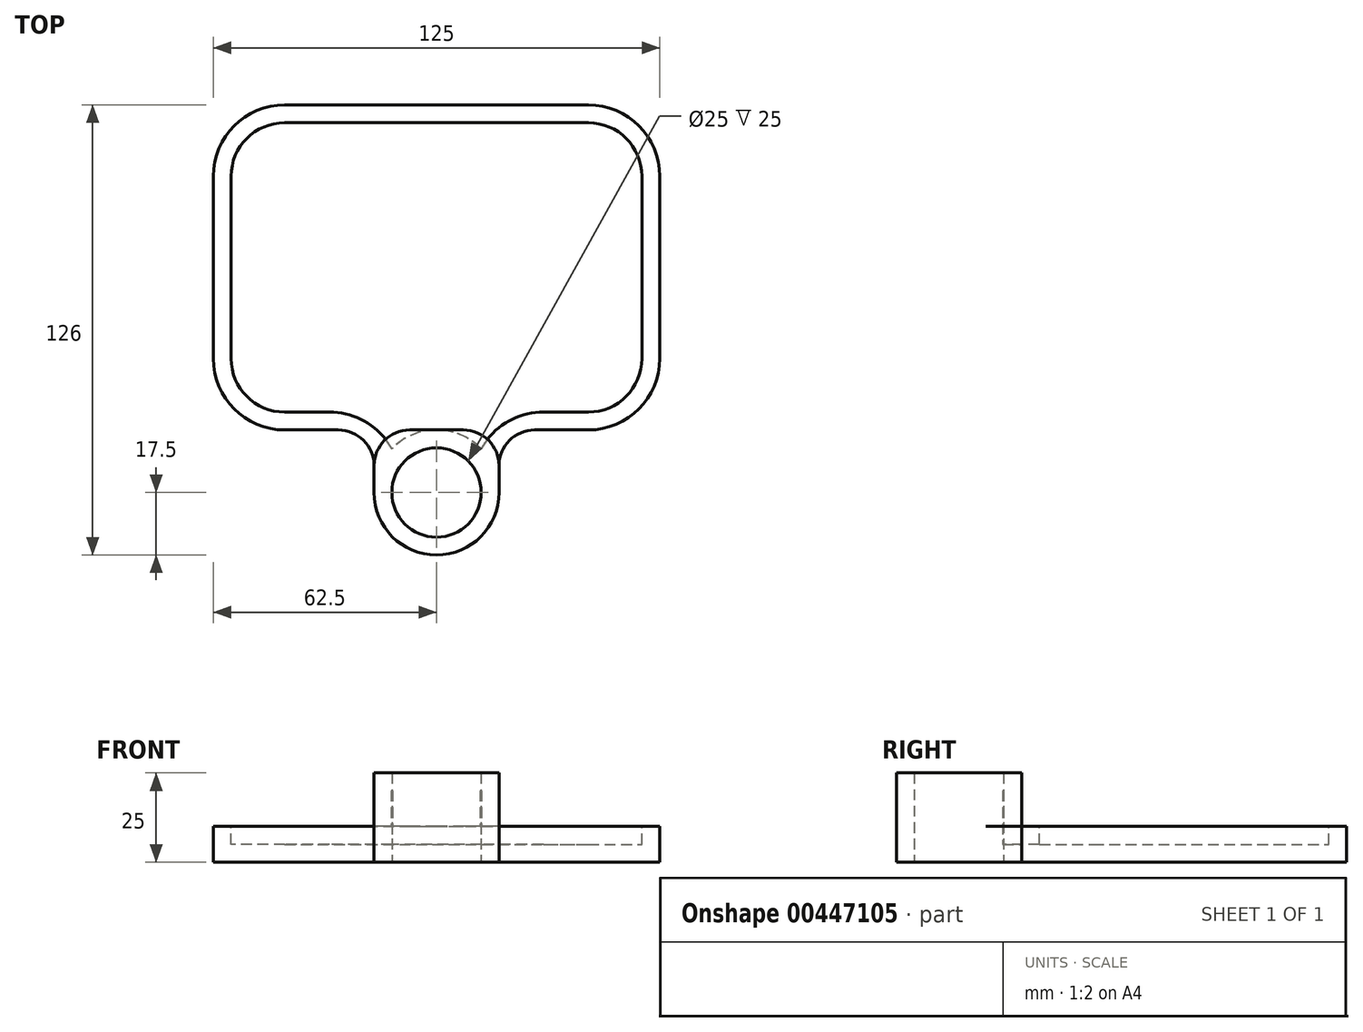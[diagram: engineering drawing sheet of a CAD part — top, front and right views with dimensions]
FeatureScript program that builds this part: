
annotation { "Feature Type Name" : "Feature", "Feature Type Description" : "" }
export const myFeature = defineFeature(function(context is Context, id is Id, definition is map)
    precondition{}
    {
        {
            var Q0;
            Q0=qCreatedBy(makeId("Top.planeOp"),FACE);
            var sketch = newSketch(context, id + "F0", { "sketchPlane" : qUnion([Q0])});
            skLineSegment(sketch, "E0.bottom", {"start": v(0, 0) * mm, "end": v(-62.5, 0) * mm, "construction": true});
            skLineSegment(sketch, "E0.top", {"start": v(0, 108.5) * mm, "end": v(-42.5, 108.5) * mm});
            skLineSegment(sketch, "E0.left", {"start": v(0, 0) * mm, "end": v(0, 108.5) * mm, "construction": true});
            skLineSegment(sketch, "E0.right", {"start": v(-62.5, 37.5) * mm, "end": v(-62.5, 88.5) * mm});
            skCircle(sketch, "E1", {"center": v(0, 0) * mm, "radius": 12.5 * mm});
            skCircle(sketch, "E2", {"center": v(0, 0) * mm, "radius": 17.5 * mm});
            skLineSegment(sketch, "E3", {"start": v(0, 17.5) * mm, "end": v(-42.5, 17.5) * mm});
            skLineSegment(sketch, "E4", {"start": v(-17.5, 0) * mm, "end": v(-17.5, 17.5) * mm});
            skPoint(sketch, "E5.newPointB", {"position": v(-62.5, 0) * mm});
            skArc(sketch, "E5.filletArc", {"start": v(-62.5, 37.5) * mm, "mid": v(-56.64, 23.36) * mm, "end": v(-42.5, 17.5) * mm});
            skPoint(sketch, "E6.visualSharp", {"position": v(-62.5, 108.5) * mm});
            skArc(sketch, "E6.filletArc", {"start": v(-42.5, 108.5) * mm, "mid": v(-56.64, 102.64) * mm, "end": v(-62.5, 88.5) * mm});
            skLineSegment(sketch, "E7.MirrorCS", {"start": v(0, 108.5) * mm, "end": v(42.5, 108.5) * mm});
            skArc(sketch, "E8.MirrorCS", {"start": v(42.5, 108.5) * mm, "mid": v(56.64, 102.64) * mm, "end": v(62.5, 88.5) * mm});
            skLineSegment(sketch, "E9.MirrorCS", {"start": v(62.5, 37.5) * mm, "end": v(62.5, 88.5) * mm});
            skArc(sketch, "E10.MirrorCS", {"start": v(62.5, 37.5) * mm, "mid": v(56.64, 23.36) * mm, "end": v(42.5, 17.5) * mm});
            skLineSegment(sketch, "E11.MirrorCS", {"start": v(0, 17.5) * mm, "end": v(42.5, 17.5) * mm});
            skLineSegment(sketch, "E12.MirrorCS", {"start": v(17.5, 0) * mm, "end": v(17.5, 17.5) * mm});
            skSolve(sketch);
        }
        {
            var Q0;
            {var subQ3=sQuery(id+"F0.wireOp",EDGE,"E12.MirrorCS");Q0=makeQuery(id+"F0.imprint","IMPRINT",FACE,{"disambiguationData":[TD([[makeQuery(id+"F0.imprint","IMPRINT",EDGE,{"derivedFrom":subQ3}),1.0]])]});}
            var Q1;
            {var subQ3=sQuery(id+"F0.wireOp",EDGE,"E4");Q1=makeQuery(id+"F0.imprint","IMPRINT",FACE,{"disambiguationData":[TD([[makeQuery(id+"F0.imprint","IMPRINT",EDGE,{"derivedFrom":subQ3}),-1.0]])]});}
            var Q2;
            Q2=makeQuery(id+"F0.imprint","IMPRINT",FACE,{"disambiguationData":[TD([[makeQuery(id+"F0.imprint","IMPRINT",EDGE,{"derivedFrom":sQuery(id+"F0.wireOp",EDGE,"E1")}),-1.0]])]});
            var Q3;
            Q3=makeQuery(id+"F0.imprint","IMPRINT",FACE,{"disambiguationData":[TD([[makeQuery(id+"F0.imprint","IMPRINT",EDGE,{"derivedFrom":sQuery(id+"F0.wireOp",EDGE,"E0.top")}),1.0]])]});
            var Q4;
            {var subQ3=sQuery(id+"F0.wireOp",EDGE,"E12.MirrorCS");Q4=makeQuery(id+"F0.imprint","IMPRINT",FACE,{"disambiguationData":[TD([[makeQuery(id+"F0.imprint","IMPRINT",EDGE,{"derivedFrom":subQ3}),1.0]])]});}
            var Q5;
            {var subQ3=sQuery(id+"F0.wireOp",EDGE,"E4");Q5=makeQuery(id+"F0.imprint","IMPRINT",FACE,{"disambiguationData":[TD([[makeQuery(id+"F0.imprint","IMPRINT",EDGE,{"derivedFrom":subQ3}),-1.0]])]});}
            var Q6;
            Q6=makeQuery(id+"F0.imprint","IMPRINT",FACE,{"disambiguationData":[TD([[makeQuery(id+"F0.imprint","IMPRINT",EDGE,{"derivedFrom":sQuery(id+"F0.wireOp",EDGE,"E1")}),-1.0]])]});
            extrude(context, id + "F1", {"entities" : qUnion([Q0, Q1, Q2, Q3, Q4, Q5, Q6]), "depth" : 10 * mm});
        }
        {
            var Q0;
            Q0=makeQuery(id+"F1.opExtrude","CAP_FACE",FACE,{"disambiguationData":[OSD([sQuery(id+"F0.wireOp",EDGE,"E0.top"),sQuery(id+"F0.wireOp",EDGE,"E0.right"),sQuery(id+"F0.wireOp",EDGE,"E1"),sQuery(id+"F0.wireOp",EDGE,"E2"),sQuery(id+"F0.wireOp",EDGE,"E3"),sQuery(id+"F0.wireOp",EDGE,"E4"),sQuery(id+"F0.wireOp",EDGE,"E5.filletArc"),sQuery(id+"F0.wireOp",EDGE,"E6.filletArc"),sQuery(id+"F0.wireOp",EDGE,"E7.MirrorCS"),sQuery(id+"F0.wireOp",EDGE,"E8.MirrorCS"),sQuery(id+"F0.wireOp",EDGE,"E9.MirrorCS"),sQuery(id+"F0.wireOp",EDGE,"E10.MirrorCS"),sQuery(id+"F0.wireOp",EDGE,"E11.MirrorCS"),sQuery(id+"F0.wireOp",EDGE,"E12.MirrorCS")])],"isStart":false});
            var sketch = newSketch(context, id + "F2", { "sketchPlane" : qUnion([Q0])});
            skLineSegment(sketch, "E13", {"start": v(-17.5, 17.5) * mm, "end": v(17.5, 17.5) * mm});
            skSolve(sketch);
        }
        {
            var Q0;
            Q0=makeQuery(id+"F2.imprint","IMPRINT",FACE,{"disambiguationData":[TD([[makeQuery(id+"F2.imprint","IMPRINT",EDGE,{"derivedFrom":sQuery(id+"F2.wireOp",EDGE,"E13")}),-1.0]])]});
            extrude(context, id + "F3", {"entities" : qUnion([Q0]), "operationType" : NewBodyOperationType.ADD, "depth" : 15 * mm});
        }
        {
            var Q0;
            Q0=makeQuery(id+"F1.opExtrude","CAP_FACE",FACE,{"disambiguationData":[OSD([sQuery(id+"F0.wireOp",EDGE,"E0.top"),sQuery(id+"F0.wireOp",EDGE,"E0.right"),sQuery(id+"F0.wireOp",EDGE,"E1"),sQuery(id+"F0.wireOp",EDGE,"E2"),sQuery(id+"F0.wireOp",EDGE,"E3"),sQuery(id+"F0.wireOp",EDGE,"E4"),sQuery(id+"F0.wireOp",EDGE,"E5.filletArc"),sQuery(id+"F0.wireOp",EDGE,"E6.filletArc"),sQuery(id+"F0.wireOp",EDGE,"E7.MirrorCS"),sQuery(id+"F0.wireOp",EDGE,"E8.MirrorCS"),sQuery(id+"F0.wireOp",EDGE,"E9.MirrorCS"),sQuery(id+"F0.wireOp",EDGE,"E10.MirrorCS"),sQuery(id+"F0.wireOp",EDGE,"E11.MirrorCS"),sQuery(id+"F0.wireOp",EDGE,"E12.MirrorCS")])],"isStart":false});
            shell(context, id + "F4", {"entities" : qUnion([Q0]), "thickness" : 5 * mm});
        }
        {
            var Q0;
            Q0=makeQuery(id+"F1.opExtrude","SWEPT_EDGE",EDGE,{"disambiguationData":[OSD([sQuery(id+"F0.wireOp",EDGE,"E11.MirrorCS"),sQuery(id+"F0.wireOp",EDGE,"E12.MirrorCS")])]});
            var Q1;
            Q1=makeQuery(id+"F1.opExtrude","SWEPT_EDGE",EDGE,{"disambiguationData":[OSD([sQuery(id+"F0.wireOp",EDGE,"E3"),sQuery(id+"F0.wireOp",EDGE,"E4")])]});
            fillet(context, id + "F5", {"entities" : qUnion([Q0, Q1]), "radius" : 10 * mm, "tangentPropagation" : true, "allowEdgeOverflow" : false});
        }
        {
            var Q0;
            Q0=makeQuery(id+"F3.opExtrude","SWEPT_EDGE",EDGE,{"disambiguationData":[OSD([sQuery(id+"F0.wireOp",EDGE,"E11.MirrorCS"),sQuery(id+"F0.wireOp",EDGE,"E12.MirrorCS"),sQuery(id+"F2.wireOp",EDGE,"E13")])]});
            var Q1;
            Q1=makeQuery(id+"F3.opExtrude","SWEPT_EDGE",EDGE,{"disambiguationData":[OSD([sQuery(id+"F0.wireOp",EDGE,"E3"),sQuery(id+"F0.wireOp",EDGE,"E4"),sQuery(id+"F2.wireOp",EDGE,"E13")])]});
            fillet(context, id + "F6", {"entities" : qUnion([Q0, Q1]), "radius" : 10 * mm, "allowEdgeOverflow" : false});
        }
        {
            var Q0;
            Q0=makeQuery(id+"F4.opShell","OFFSET_EDGE",EDGE,{"disambiguationData":[OSD([sQuery(id+"F0.wireOp",EDGE,"E11.MirrorCS"),sQuery(id+"F0.wireOp",EDGE,"E12.MirrorCS")])]});
            var Q1;
            Q1=makeQuery(id+"F4.opShell","OFFSET_EDGE",EDGE,{"disambiguationData":[OSD([sQuery(id+"F0.wireOp",EDGE,"E3"),sQuery(id+"F0.wireOp",EDGE,"E4")])]});
            fillet(context, id + "F7", {"entities" : qUnion([Q0, Q1]), "radius" : 20 * mm, "tangentPropagation" : true, "allowEdgeOverflow" : false});
        }
    });
